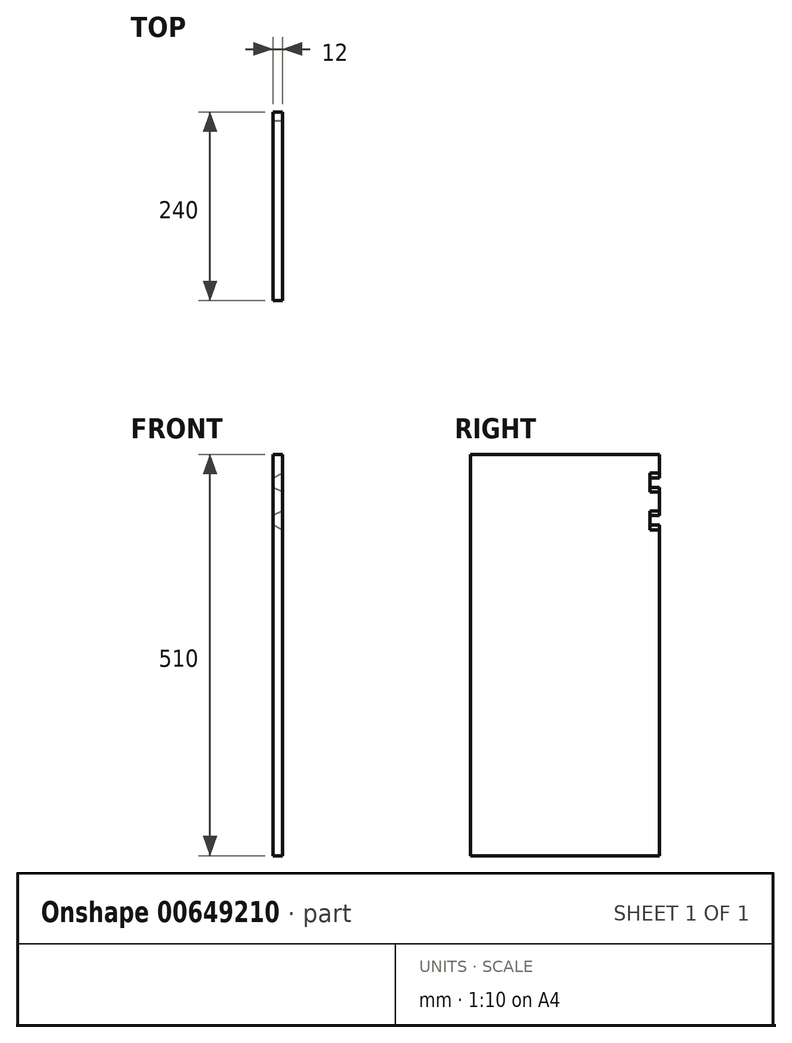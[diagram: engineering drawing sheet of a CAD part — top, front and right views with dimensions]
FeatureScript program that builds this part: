
annotation { "Feature Type Name" : "Feature", "Feature Type Description" : "" }
export const myFeature = defineFeature(function(context is Context, id is Id, definition is map)
    precondition{}
    {
        {
            var Q0;
            Q0=qCreatedBy(makeId("Right.planeOp"),FACE);
            var sketch = newSketch(context, id + "F0", { "sketchPlane" : qUnion([Q0])});
            skLineSegment(sketch, "E0.bottom", {"start": v(120, 261) * mm, "end": v(-120, 261) * mm});
            skLineSegment(sketch, "E0.top", {"start": v(120, -261) * mm, "end": v(-120, -261) * mm});
            skLineSegment(sketch, "E0.left", {"start": v(120, 261) * mm, "end": v(120, -261) * mm});
            skLineSegment(sketch, "E0.right", {"start": v(-120, 261) * mm, "end": v(-120, -261) * mm});
            skPoint(sketch, "E0.middle", {"position": v(0, 0) * mm});
            skLineSegment(sketch, "E1", {"start": v(108, 261) * mm, "end": v(108, -261) * mm, "construction": true});
            skLineSegment(sketch, "E2", {"start": v(108, 254.77) * mm, "end": v(120, 254.77) * mm, "construction": true});
            skLineSegment(sketch, "E3", {"start": v(120, 249) * mm, "end": v(-120, 249) * mm, "construction": true});
            skLineSegment(sketch, "E4", {"start": v(-118, 261) * mm, "end": v(-118, 249) * mm, "construction": true});
            skLineSegment(sketch, "E5.bottom", {"start": v(-96, 261) * mm, "end": v(-72, 261) * mm});
            skLineSegment(sketch, "E5.top", {"start": v(-96, 249) * mm, "end": v(-72, 249) * mm});
            skLineSegment(sketch, "E5.left", {"start": v(-96, 261) * mm, "end": v(-96, 249) * mm});
            skLineSegment(sketch, "E5.right", {"start": v(-72, 261) * mm, "end": v(-72, 249) * mm});
            skLineSegment(sketch, "E6.bottom", {"start": v(-48, 261) * mm, "end": v(-24, 261) * mm});
            skLineSegment(sketch, "E6.top", {"start": v(-48, 249) * mm, "end": v(-24, 249) * mm});
            skLineSegment(sketch, "E6.left", {"start": v(-48, 261) * mm, "end": v(-48, 249) * mm});
            skLineSegment(sketch, "E6.right", {"start": v(-24, 261) * mm, "end": v(-24, 249) * mm});
            skLineSegment(sketch, "E7.bottom", {"start": v(24, 261) * mm, "end": v(48, 261) * mm});
            skLineSegment(sketch, "E7.top", {"start": v(24, 249) * mm, "end": v(48, 249) * mm});
            skLineSegment(sketch, "E7.left", {"start": v(24, 261) * mm, "end": v(24, 249) * mm});
            skLineSegment(sketch, "E7.right", {"start": v(48, 261) * mm, "end": v(48, 249) * mm});
            skLineSegment(sketch, "E8.bottom", {"start": v(72, 261) * mm, "end": v(96, 261) * mm});
            skLineSegment(sketch, "E8.top", {"start": v(72, 249) * mm, "end": v(96, 249) * mm});
            skLineSegment(sketch, "E8.left", {"start": v(72, 261) * mm, "end": v(72, 249) * mm});
            skLineSegment(sketch, "E8.right", {"start": v(96, 261) * mm, "end": v(96, 249) * mm});
            skLineSegment(sketch, "E9", {"start": v(120, 252.12) * mm, "end": v(96, 252.12) * mm, "construction": true});
            skLineSegment(sketch, "E10", {"start": v(72, 255) * mm, "end": v(48, 255) * mm, "construction": true});
            skLineSegment(sketch, "E11", {"start": v(-48, 255) * mm, "end": v(-72, 255) * mm, "construction": true});
            skLineSegment(sketch, "E12", {"start": v(-96, 255) * mm, "end": v(-120, 255) * mm, "construction": true});
            skLineSegment(sketch, "E13", {"start": v(-96, 261) * mm, "end": v(-90, 249) * mm});
            skLineSegment(sketch, "E14", {"start": v(-90, 249) * mm, "end": v(-96, 249) * mm});
            skLineSegment(sketch, "E15", {"start": v(-72, 261) * mm, "end": v(-78, 249) * mm});
            skLineSegment(sketch, "E16", {"start": v(-78, 249) * mm, "end": v(-72, 249) * mm});
            skLineSegment(sketch, "E17", {"start": v(-48, 261) * mm, "end": v(-42, 249) * mm});
            skLineSegment(sketch, "E18", {"start": v(-42, 249) * mm, "end": v(-48, 249) * mm});
            skLineSegment(sketch, "E19", {"start": v(-24, 249) * mm, "end": v(-30, 249) * mm});
            skLineSegment(sketch, "E20", {"start": v(-30, 249) * mm, "end": v(-24, 261) * mm});
            skLineSegment(sketch, "E21", {"start": v(96, 261) * mm, "end": v(90, 249) * mm});
            skLineSegment(sketch, "E22", {"start": v(90, 249) * mm, "end": v(96, 249) * mm});
            skLineSegment(sketch, "E23", {"start": v(78, 249) * mm, "end": v(72, 249) * mm});
            skLineSegment(sketch, "E24", {"start": v(78, 249) * mm, "end": v(72, 261) * mm});
            skLineSegment(sketch, "E25", {"start": v(48, 261) * mm, "end": v(42, 249) * mm});
            skLineSegment(sketch, "E26", {"start": v(42, 249) * mm, "end": v(48, 249) * mm});
            skLineSegment(sketch, "E27", {"start": v(24, 249) * mm, "end": v(30, 249) * mm});
            skLineSegment(sketch, "E28", {"start": v(30, 249) * mm, "end": v(24, 261) * mm});
            skLineSegment(sketch, "E29", {"start": v(96, 249) * mm, "end": v(120, 249) * mm});
            skLineSegment(sketch, "E30", {"start": v(72, 249) * mm, "end": v(48, 249) * mm});
            skLineSegment(sketch, "E31", {"start": v(24, 249) * mm, "end": v(-24, 249) * mm});
            skLineSegment(sketch, "E32", {"start": v(-48, 249) * mm, "end": v(-72, 249) * mm});
            skLineSegment(sketch, "E33", {"start": v(-96, 249) * mm, "end": v(-120, 249) * mm});
            skLineSegment(sketch, "E34", {"start": v(114, 249) * mm, "end": v(114, 225) * mm, "construction": true});
            skLineSegment(sketch, "E35.bottom", {"start": v(120, 225) * mm, "end": v(108, 225) * mm});
            skLineSegment(sketch, "E35.top", {"start": v(120, 201) * mm, "end": v(108, 201) * mm});
            skLineSegment(sketch, "E35.left", {"start": v(120, 225) * mm, "end": v(120, 201) * mm});
            skLineSegment(sketch, "E35.right", {"start": v(108, 225) * mm, "end": v(108, 201) * mm});
            skPoint(sketch, "E36", {"position": v(114, 225) * mm});
            skLineSegment(sketch, "E37.bottom", {"start": v(120, 177) * mm, "end": v(108, 177) * mm});
            skLineSegment(sketch, "E37.top", {"start": v(120, 153) * mm, "end": v(108, 153) * mm});
            skLineSegment(sketch, "E37.left", {"start": v(120, 177) * mm, "end": v(120, 153) * mm});
            skLineSegment(sketch, "E37.right", {"start": v(108, 177) * mm, "end": v(108, 153) * mm});
            skLineSegment(sketch, "E38", {"start": v(114, 201) * mm, "end": v(114, 177) * mm, "construction": true});
            skSolve(sketch);
        }
        {
            var Q0;
            {var subQ0=sQuery(id+"F0.wireOp",EDGE,"E0.top");Q0=makeQuery(id+"F0.imprint","IMPRINT",FACE,{"disambiguationData":[TD([[makeQuery(id+"F0.imprint","IMPRINT",EDGE,{"derivedFrom":subQ0}),-1.0]])]});}
            var Q1;
            Q1=makeQuery(id+"F0.imprint","IMPRINT",FACE,{"disambiguationData":[TD([[makeQuery(id+"F0.imprint","IMPRINT",EDGE,{"derivedFrom":sQuery(id+"F0.wireOp",EDGE,"E5.bottom")}),-1.0]])]});
            var Q2;
            Q2=makeQuery(id+"F0.imprint","IMPRINT",FACE,{"disambiguationData":[TD([[makeQuery(id+"F0.imprint","IMPRINT",EDGE,{"derivedFrom":sQuery(id+"F0.wireOp",EDGE,"E6.bottom")}),-1.0]])]});
            var Q3;
            Q3=makeQuery(id+"F0.imprint","IMPRINT",FACE,{"disambiguationData":[TD([[makeQuery(id+"F0.imprint","IMPRINT",EDGE,{"derivedFrom":sQuery(id+"F0.wireOp",EDGE,"E7.bottom")}),-1.0]])]});
            var Q4;
            Q4=makeQuery(id+"F0.imprint","IMPRINT",FACE,{"disambiguationData":[TD([[makeQuery(id+"F0.imprint","IMPRINT",EDGE,{"derivedFrom":sQuery(id+"F0.wireOp",EDGE,"E8.bottom")}),-1.0]])]});
            extrude(context, id + "F1", {"entities" : qUnion([Q0, Q1, Q2, Q3, Q4]), "depth" : 12 * mm, "offsetDistance" : 25 * mm});
        }
        {
            var Q0;
            Q0=makeQuery(id+"F1.opExtrude","SWEPT_FACE",FACE,{"disambiguationData":[OSD([sQuery(id+"F0.wireOp",EDGE,"E35.right")])]});
            var sketch = newSketch(context, id + "F2", { "sketchPlane" : qUnion([Q0])});
            skLineSegment(sketch, "E39", {"start": v(0, 225) * mm, "end": v(0, 219) * mm});
            skLineSegment(sketch, "E40", {"start": v(0, 219) * mm, "end": v(-12, 225) * mm});
            skLineSegment(sketch, "E41", {"start": v(-12, 225) * mm, "end": v(0, 225) * mm});
            skLineSegment(sketch, "E42", {"start": v(-12, 201) * mm, "end": v(0, 207) * mm});
            skLineSegment(sketch, "E43", {"start": v(0, 207) * mm, "end": v(0, 201) * mm});
            skLineSegment(sketch, "E44", {"start": v(0, 201) * mm, "end": v(-12, 201) * mm});
            skSolve(sketch);
        }
        {
            var Q0;
            Q0=qSketchRegion(id+"F2",true);
            extrude(context, id + "F3", {"entities" : qUnion([Q0]), "operationType" : NewBodyOperationType.ADD, "depth" : 12 * mm, "offsetDistance" : 25 * mm});
        }
        {
            var Q0;
            Q0=makeQuery(id+"F1.opExtrude","SWEPT_FACE",FACE,{"disambiguationData":[OSD([sQuery(id+"F0.wireOp",EDGE,"E37.right")])]});
            var sketch = newSketch(context, id + "F4", { "sketchPlane" : qUnion([Q0])});
            skLineSegment(sketch, "E45", {"start": v(-12, 177) * mm, "end": v(0, 171) * mm});
            skLineSegment(sketch, "E46", {"start": v(0, 171) * mm, "end": v(0, 177) * mm});
            skLineSegment(sketch, "E47", {"start": v(0, 177) * mm, "end": v(-12, 177) * mm});
            skLineSegment(sketch, "E48", {"start": v(-12, 153) * mm, "end": v(0, 159) * mm});
            skLineSegment(sketch, "E49", {"start": v(0, 159) * mm, "end": v(0, 153) * mm});
            skLineSegment(sketch, "E50", {"start": v(0, 153) * mm, "end": v(-12, 153) * mm});
            skSolve(sketch);
        }
        {
            var Q0;
            Q0 = qSketchRegion(id + "F4", true);
            extrude(context, id + "F5", {"entities" : qUnion([Q0]), "operationType" : NewBodyOperationType.ADD, "depth" : 12 * mm, "offsetDistance" : 25 * mm});
        }
    });
